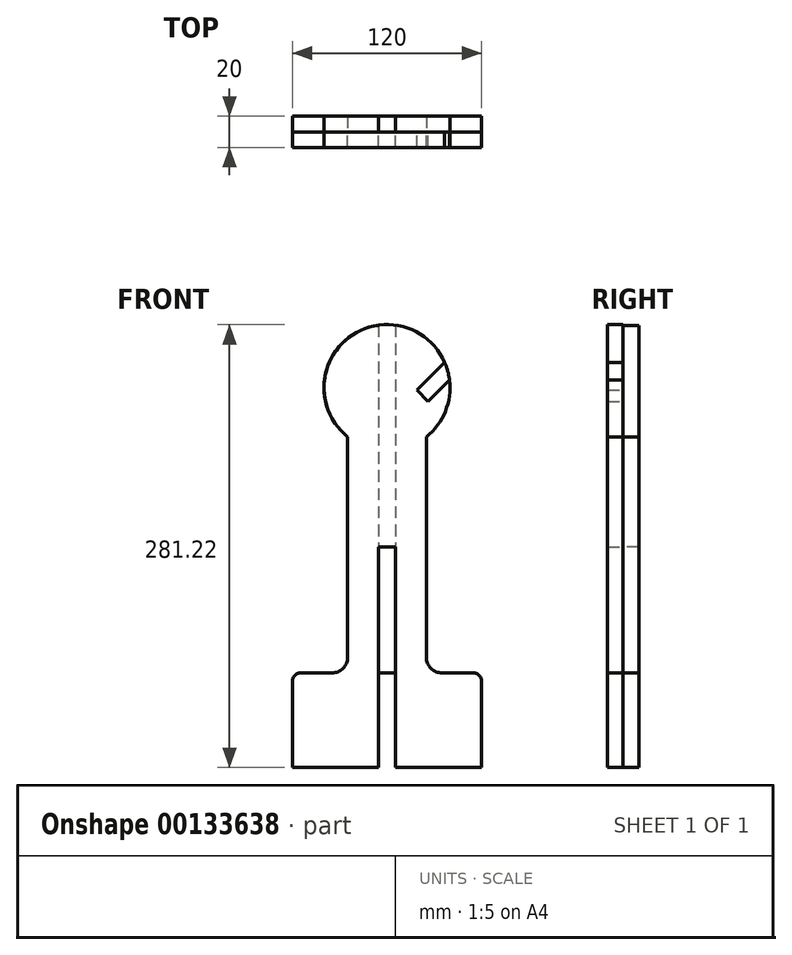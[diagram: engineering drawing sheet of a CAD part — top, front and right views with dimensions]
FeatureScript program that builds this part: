
annotation { "Feature Type Name" : "Feature", "Feature Type Description" : "" }
export const myFeature = defineFeature(function(context is Context, id is Id, definition is map)
    precondition{}
    {
        {
            var Q0;
            Q0=qCreatedBy(makeId("Front.planeOp"),FACE);
            var sketch = newSketch(context, id + "F0", { "sketchPlane" : qUnion([Q0])});
            skCircle(sketch, "E0", {"center": v(0, 0) * mm, "radius": 40 * mm});
            skLineSegment(sketch, "E1.bottom", {"start": v(-25, -31.22) * mm, "end": v(25, -31.22) * mm});
            skLineSegment(sketch, "E1.top", {"start": v(-25, -181.22) * mm, "end": v(25, -181.22) * mm});
            skLineSegment(sketch, "E1.left", {"start": v(-25, -31.22) * mm, "end": v(-25, -171.22) * mm});
            skLineSegment(sketch, "E1.right", {"start": v(25, -31.22) * mm, "end": v(25, -171.22) * mm});
            skPoint(sketch, "E1.middle", {"position": v(0, -106.22) * mm});
            skLineSegment(sketch, "E2.bottom", {"start": v(-35, -181.22) * mm, "end": v(-55, -181.22) * mm});
            skLineSegment(sketch, "E2.top", {"start": v(60, -241.22) * mm, "end": v(-60, -241.22) * mm});
            skLineSegment(sketch, "E2.left", {"start": v(60, -186.22) * mm, "end": v(60, -241.22) * mm});
            skLineSegment(sketch, "E2.right", {"start": v(-60, -186.22) * mm, "end": v(-60, -241.22) * mm});
            skPoint(sketch, "E2.middle", {"position": v(0, -211.22) * mm});
            skPoint(sketch, "E2.cornerSnap0", {"position": v(0, -181.22) * mm});
            skLineSegment(sketch, "E3.bottom", {"start": v(-5.5, 39.62) * mm, "end": v(5.5, 39.62) * mm});
            skLineSegment(sketch, "E3.top", {"start": v(-5.5, -101.22) * mm, "end": v(5.5, -101.22) * mm});
            skLineSegment(sketch, "E3.left", {"start": v(-5.5, 39.62) * mm, "end": v(-5.5, -101.22) * mm});
            skLineSegment(sketch, "E3.right", {"start": v(5.5, 39.62) * mm, "end": v(5.5, -101.22) * mm});
            skPoint(sketch, "E3.middle", {"position": v(0, -30.8) * mm});
            skLineSegment(sketch, "E4.top", {"start": v(-5.5, -241.22) * mm, "end": v(5.5, -241.22) * mm});
            skLineSegment(sketch, "E4.left", {"start": v(-5.5, -101.22) * mm, "end": v(-5.5, -241.22) * mm});
            skLineSegment(sketch, "E4.right", {"start": v(5.5, -101.22) * mm, "end": v(5.5, -241.22) * mm});
            skPoint(sketch, "E4.middle", {"position": v(0, -171.22) * mm});
            skLineSegment(sketch, "E5", {"start": v(36.63, 16.08) * mm, "end": v(18.95, -1.6) * mm});
            skLineSegment(sketch, "E6", {"start": v(18.95, -1.6) * mm, "end": v(26.02, -8.67) * mm});
            skLineSegment(sketch, "E7", {"start": v(26.02, -8.67) * mm, "end": v(39.69, 5) * mm});
            skPoint(sketch, "E8.visualSharp", {"position": v(-60, -181.22) * mm});
            skArc(sketch, "E8.filletArc", {"start": v(-55, -181.22) * mm, "mid": v(-58.54, -182.69) * mm, "end": v(-60, -186.22) * mm});
            skPoint(sketch, "E9.visualSharp", {"position": v(60, -181.22) * mm});
            skArc(sketch, "E9.filletArc", {"start": v(60, -186.22) * mm, "mid": v(58.54, -182.69) * mm, "end": v(55, -181.22) * mm});
            skArc(sketch, "E10.filletArc", {"start": v(-35, -181.22) * mm, "mid": v(-27.93, -178.3) * mm, "end": v(-25, -171.22) * mm});
            skLineSegment(sketch, "E11", {"start": v(60, -181.22) * mm, "end": v(35, -181.22) * mm});
            skPoint(sketch, "E12.visualSharp", {"position": v(25, -181.22) * mm});
            skArc(sketch, "E12.filletArc", {"start": v(25, -171.22) * mm, "mid": v(27.93, -178.3) * mm, "end": v(35, -181.22) * mm});
            skSolve(sketch);
        }
        {
            var Q0;
            {var subQ0=sQuery(id+"F0.wireOp",EDGE,"E3.bottom");Q0=makeQuery(id+"F0.imprint","IMPRINT",FACE,{"disambiguationData":[TD([[makeQuery(id+"F0.imprint","IMPRINT",EDGE,{"derivedFrom":subQ0}),1.0]])]});}
            var Q1;
            {var subQ0=sQuery(id+"F0.wireOp",EDGE,"E1.bottom");var subQ3=sQuery(id+"F0.wireOp",EDGE,"E3.left");var subQ5=makeQuery(id+"F0.imprint","INTERSECT",VERTEX,{"derivedFrom":[subQ0,subQ3]});Q1=makeQuery(id+"F0.imprint","IMPRINT",FACE,{"disambiguationData":[TD([[makeQuery(id+"F0.imprint","IMPRINT",EDGE,{"disambiguationData":[TD([[subQ5,1.0]])],"derivedFrom":subQ0}),1.0]])]});}
            var Q2;
            {var subQ7=sQuery(id+"F0.wireOp",EDGE,"E5");Q2=makeQuery(id+"F0.imprint","IMPRINT",FACE,{"disambiguationData":[TD([[makeQuery(id+"F0.imprint","IMPRINT",EDGE,{"derivedFrom":subQ7}),-1.0]])]});}
            var Q3;
            {var subQ1=sQuery(id+"F0.wireOp",EDGE,"E0");var subQ3=sQuery(id+"F0.wireOp",EDGE,"E3.left");var subQ4=makeQuery(id+"F0.imprint","INTERSECT",VERTEX,{"derivedFrom":[subQ1,subQ3]});Q3=makeQuery(id+"F0.imprint","IMPRINT",FACE,{"disambiguationData":[TD([[makeQuery(id+"F0.imprint","IMPRINT",EDGE,{"disambiguationData":[TD([[subQ4,1.0]])],"derivedFrom":subQ3}),-1.0]])]});}
            var Q4;
            {var subQ1=sQuery(id+"F0.wireOp",EDGE,"E0");var subQ3=sQuery(id+"F0.wireOp",EDGE,"E3.right");var subQ4=makeQuery(id+"F0.imprint","INTERSECT",VERTEX,{"derivedFrom":[subQ1,subQ3]});Q4=makeQuery(id+"F0.imprint","IMPRINT",FACE,{"disambiguationData":[TD([[makeQuery(id+"F0.imprint","IMPRINT",EDGE,{"disambiguationData":[TD([[subQ4,1.0]])],"derivedFrom":subQ3}),1.0]])]});}
            var Q5;
            {var subQ4=sQuery(id+"F0.wireOp",EDGE,"E1.left");Q5=makeQuery(id+"F0.imprint","IMPRINT",FACE,{"disambiguationData":[TD([[makeQuery(id+"F0.imprint","IMPRINT",EDGE,{"derivedFrom":subQ4}),1.0]])]});}
            var Q6;
            {var subQ1=sQuery(id+"F0.wireOp",EDGE,"E1.right");Q6=makeQuery(id+"F0.imprint","IMPRINT",FACE,{"disambiguationData":[TD([[makeQuery(id+"F0.imprint","IMPRINT",EDGE,{"derivedFrom":subQ1}),-1.0]])]});}
            var Q7;
            {var subQ5=sQuery(id+"F0.wireOp",EDGE,"E3.bottom");Q7=makeQuery(id+"F0.imprint","IMPRINT",FACE,{"disambiguationData":[TD([[makeQuery(id+"F0.imprint","IMPRINT",EDGE,{"derivedFrom":subQ5}),-1.0]])]});}
            var Q8;
            {var subQ5=sQuery(id+"F0.wireOp",EDGE,"E3.top");Q8=makeQuery(id+"F0.imprint","IMPRINT",FACE,{"disambiguationData":[TD([[makeQuery(id+"F0.imprint","IMPRINT",EDGE,{"derivedFrom":subQ5}),1.0]])]});}
            var Q9;
            {var subQ0=sQuery(id+"F0.wireOp",EDGE,"E3.left");var subQ1=sQuery(id+"F0.wireOp",EDGE,"E0");var subQ2=makeQuery(id+"F0.imprint","INTERSECT",VERTEX,{"derivedFrom":[subQ1,subQ0]});Q9=makeQuery(id+"F0.imprint","IMPRINT",FACE,{"disambiguationData":[TD([[makeQuery(id+"F0.imprint","IMPRINT",EDGE,{"disambiguationData":[TD([[subQ2,-1.0]])],"derivedFrom":subQ1}),1.0]])]});}
            extrude(context, id + "F1", {"entities" : qUnion([Q0, Q1, Q2, Q3, Q4, Q5, Q6, Q7, Q8, Q9]), "depth" : 10 * mm});
        }
        {
            var Q0;
            {var subQ7=sQuery(id+"F0.wireOp",EDGE,"E5");Q0=makeQuery(id+"F0.imprint","IMPRINT",FACE,{"disambiguationData":[TD([[makeQuery(id+"F0.imprint","IMPRINT",EDGE,{"derivedFrom":subQ7}),-1.0]])]});}
            var Q1;
            {var subQ0=sQuery(id+"F0.wireOp",EDGE,"E5");Q1=makeQuery(id+"F0.imprint","IMPRINT",FACE,{"disambiguationData":[TD([[makeQuery(id+"F0.imprint","IMPRINT",EDGE,{"derivedFrom":subQ0}),1.0]])]});}
            var Q2;
            {var subQ0=sQuery(id+"F0.wireOp",EDGE,"E1.bottom");var subQ3=sQuery(id+"F0.wireOp",EDGE,"E3.left");var subQ5=makeQuery(id+"F0.imprint","INTERSECT",VERTEX,{"derivedFrom":[subQ0,subQ3]});Q2=makeQuery(id+"F0.imprint","IMPRINT",FACE,{"disambiguationData":[TD([[makeQuery(id+"F0.imprint","IMPRINT",EDGE,{"disambiguationData":[TD([[subQ5,1.0]])],"derivedFrom":subQ0}),1.0]])]});}
            var Q3;
            {var subQ1=sQuery(id+"F0.wireOp",EDGE,"E0");var subQ3=sQuery(id+"F0.wireOp",EDGE,"E3.left");var subQ4=makeQuery(id+"F0.imprint","INTERSECT",VERTEX,{"derivedFrom":[subQ1,subQ3]});Q3=makeQuery(id+"F0.imprint","IMPRINT",FACE,{"disambiguationData":[TD([[makeQuery(id+"F0.imprint","IMPRINT",EDGE,{"disambiguationData":[TD([[subQ4,1.0]])],"derivedFrom":subQ3}),-1.0]])]});}
            var Q4;
            {var subQ1=sQuery(id+"F0.wireOp",EDGE,"E0");var subQ3=sQuery(id+"F0.wireOp",EDGE,"E3.right");var subQ4=makeQuery(id+"F0.imprint","INTERSECT",VERTEX,{"derivedFrom":[subQ1,subQ3]});Q4=makeQuery(id+"F0.imprint","IMPRINT",FACE,{"disambiguationData":[TD([[makeQuery(id+"F0.imprint","IMPRINT",EDGE,{"disambiguationData":[TD([[subQ4,1.0]])],"derivedFrom":subQ3}),1.0]])]});}
            var Q5;
            {var subQ1=sQuery(id+"F0.wireOp",EDGE,"E1.right");Q5=makeQuery(id+"F0.imprint","IMPRINT",FACE,{"disambiguationData":[TD([[makeQuery(id+"F0.imprint","IMPRINT",EDGE,{"derivedFrom":subQ1}),-1.0]])]});}
            var Q6;
            {var subQ4=sQuery(id+"F0.wireOp",EDGE,"E1.left");Q6=makeQuery(id+"F0.imprint","IMPRINT",FACE,{"disambiguationData":[TD([[makeQuery(id+"F0.imprint","IMPRINT",EDGE,{"derivedFrom":subQ4}),1.0]])]});}
            var Q7;
            {var subQ5=sQuery(id+"F0.wireOp",EDGE,"E4.top");Q7=makeQuery(id+"F0.imprint","IMPRINT",FACE,{"disambiguationData":[TD([[makeQuery(id+"F0.imprint","IMPRINT",EDGE,{"derivedFrom":subQ5}),1.0]])]});}
            var Q8;
            {var subQ5=sQuery(id+"F0.wireOp",EDGE,"E3.top");Q8=makeQuery(id+"F0.imprint","IMPRINT",FACE,{"disambiguationData":[TD([[makeQuery(id+"F0.imprint","IMPRINT",EDGE,{"derivedFrom":subQ5}),-1.0]])]});}
            extrude(context, id + "F2", {"entities" : qUnion([Q0, Q1, Q2, Q3, Q4, Q5, Q6, Q7, Q8]), "oppositeDirection" : true, "depth" : 10 * mm});
        }
    });
